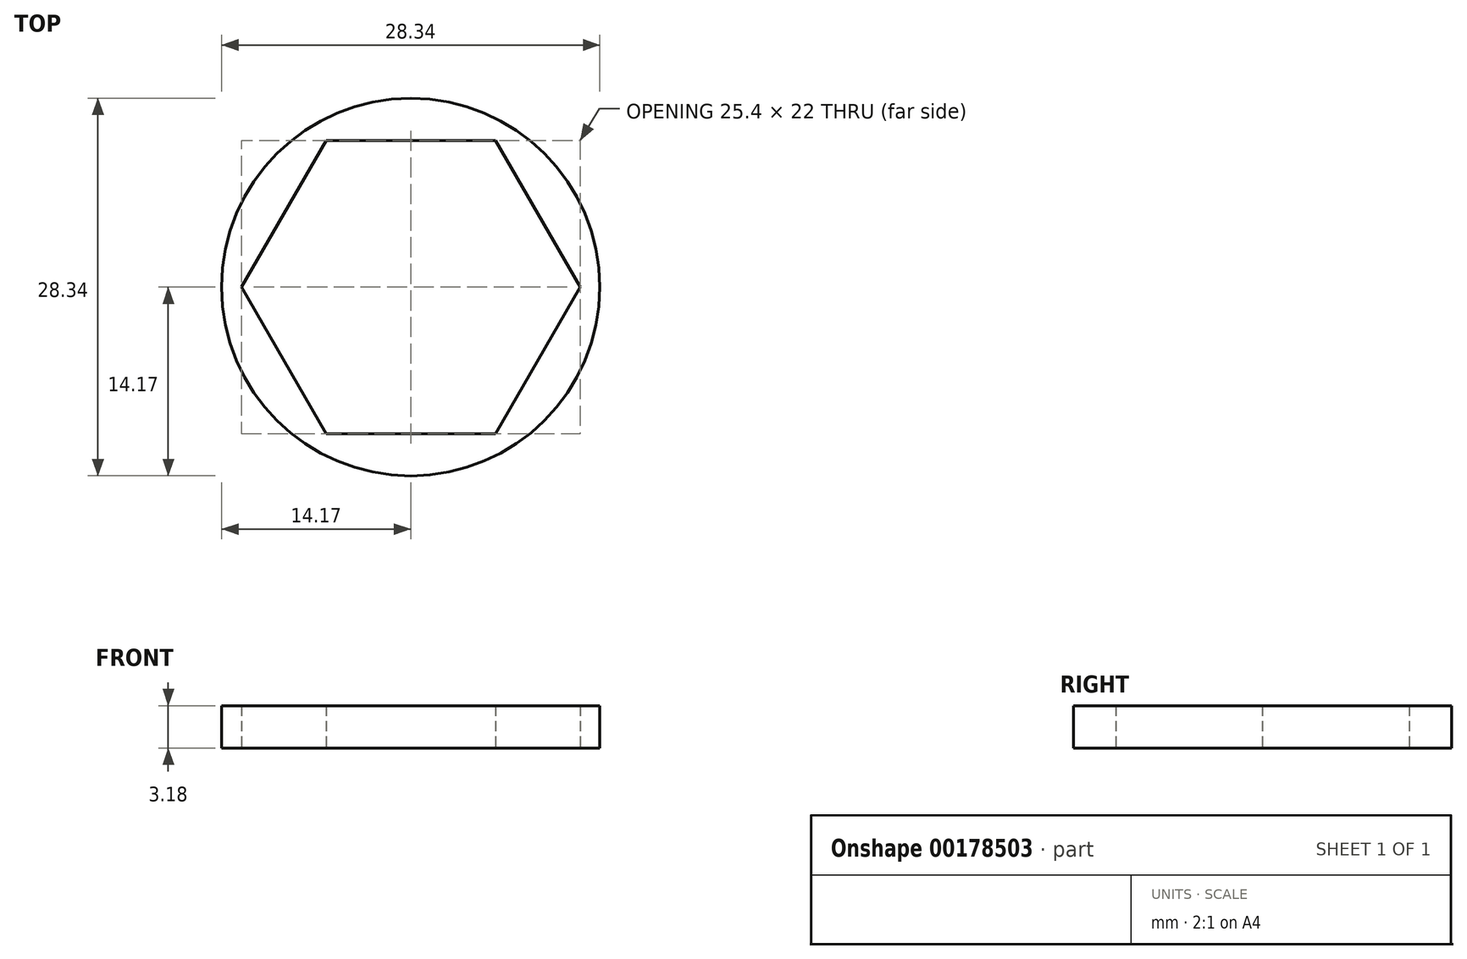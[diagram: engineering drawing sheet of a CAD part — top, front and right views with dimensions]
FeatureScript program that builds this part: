
annotation { "Feature Type Name" : "Feature", "Feature Type Description" : "" }
export const myFeature = defineFeature(function(context is Context, id is Id, definition is map)
    precondition{}
    {
        {
            var Q0;
            Q0=qCreatedBy(makeId("Top.planeOp"),FACE);
            var sketch = newSketch(context, id + "F0", { "sketchPlane" : qUnion([Q0])});
            skCircle(sketch, "E0.cCircle", {"center": v(0, 0) * mm, "radius": 11 * mm, "construction": true});
            skLineSegment(sketch, "E0.0", {"start": v(-6.35, 11) * mm, "end": v(6.35, 11) * mm});
            skLineSegment(sketch, "E0.1", {"start": v(6.35, 11) * mm, "end": v(12.7, 0) * mm});
            skLineSegment(sketch, "E0.2", {"start": v(12.7, 0) * mm, "end": v(6.35, -11) * mm});
            skLineSegment(sketch, "E0.3", {"start": v(6.35, -11) * mm, "end": v(-6.35, -11) * mm});
            skLineSegment(sketch, "E0.4", {"start": v(-6.35, -11) * mm, "end": v(-12.7, 0) * mm});
            skLineSegment(sketch, "E0.5", {"start": v(-12.7, 0) * mm, "end": v(-6.35, 11) * mm});
            skPoint(sketch, "E0.0.midPoint", {"position": v(0, 11) * mm});
            skCircle(sketch, "E1", {"center": v(0, 0) * mm, "radius": 14.17 * mm});
            skSolve(sketch);
        }
        {
            var Q0;
            Q0=makeQuery(id+"F0.imprint","IMPRINT",FACE,{"disambiguationData":[TD([[makeQuery(id+"F0.imprint","IMPRINT",EDGE,{"derivedFrom":sQuery(id+"F0.wireOp",EDGE,"E0.0")}),1.0]])]});
            extrude(context, id + "F1", {"entities" : qUnion([Q0]), "depth" : 3.17 * mm});
        }
    });
